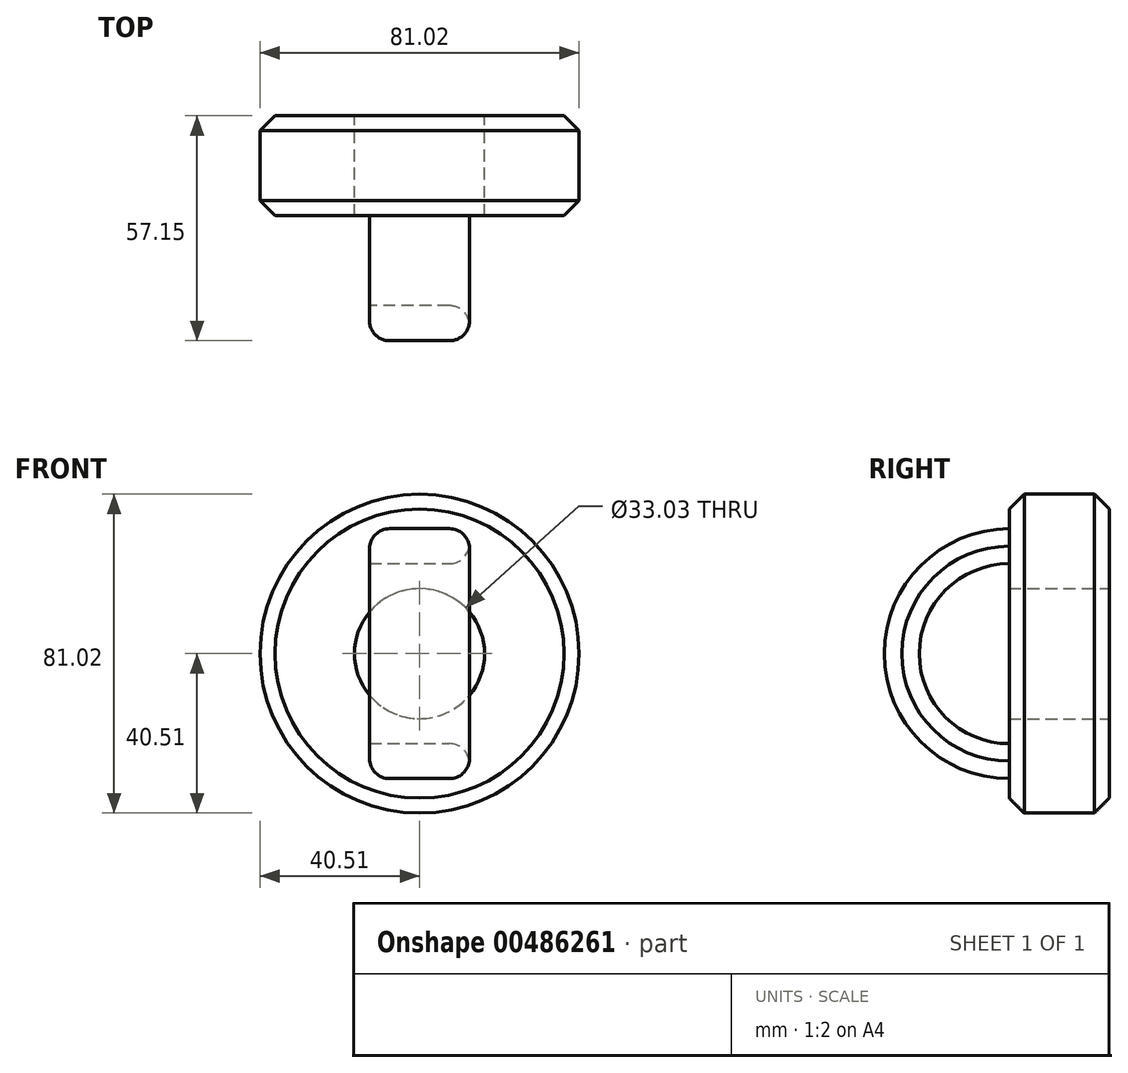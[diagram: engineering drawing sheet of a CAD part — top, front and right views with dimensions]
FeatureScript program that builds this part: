
annotation { "Feature Type Name" : "Feature", "Feature Type Description" : "" }
export const myFeature = defineFeature(function(context is Context, id is Id, definition is map)
    precondition{}
    {
        {
            var Q0;
            Q0=qCreatedBy(makeId("Front.planeOp"),FACE);
            var sketch = newSketch(context, id + "F0", { "sketchPlane" : qUnion([Q0])});
            skCircle(sketch, "E0", {"center": v(0, 0) * mm, "radius": 16.52 * mm});
            skCircle(sketch, "E1", {"center": v(0, 0) * mm, "radius": 40.51 * mm});
            skSolve(sketch);
        }
        {
            var Q0;
            Q0 = qSketchRegion(id + "F0", true);
            extrude(context, id + "F1", {"entities" : qUnion([Q0]), "depth" : 25.4 * mm});
        }
        {
            var Q0;
            Q0=makeQuery(id+"F1.opExtrude","CAP_FACE",FACE,{"disambiguationData":[OSD([sQuery(id+"F0.wireOp",EDGE,"E0"),sQuery(id+"F0.wireOp",EDGE,"E1")])],"isStart":false});
            var sketch = newSketch(context, id + "F2", { "sketchPlane" : qUnion([Q0])});
            skLineSegment(sketch, "E2.bottom", {"start": v(-12.7, 31.75) * mm, "end": v(12.7, 31.75) * mm});
            skLineSegment(sketch, "E2.top", {"start": v(-12.7, 22.86) * mm, "end": v(12.7, 22.86) * mm});
            skLineSegment(sketch, "E2.left", {"start": v(-12.7, 31.75) * mm, "end": v(-12.7, 22.86) * mm});
            skLineSegment(sketch, "E2.right", {"start": v(12.7, 31.75) * mm, "end": v(12.7, 22.86) * mm});
            skLineSegment(sketch, "E3", {"start": v(-65.94, 0) * mm, "end": v(56.87, 0) * mm});
            skLineSegment(sketch, "E4", {"start": v(56.87, 0) * mm, "end": v(0, 0) * mm});
            skSolve(sketch);
        }
        {
            var Q0;
            Q0=makeQuery(id+"F2.imprint","IMPRINT",FACE,{"disambiguationData":[TD([[makeQuery(id+"F2.imprint","IMPRINT",EDGE,{"derivedFrom":sQuery(id+"F2.wireOp",EDGE,"E2.bottom")}),-1.0]])]});
            var Q1;
            Q1=sQuery(id+"F2.wireOp",EDGE,"E3");
            revolve(context, id + "F3", {"operationType" : NewBodyOperationType.ADD, "entities" : qUnion([Q0]), "axis" : qUnion([Q1]), "revolveType" : RevolveType.ONE_DIRECTION, "angle" : 180 * degree});
        }
        {
            var Q0;
            Q0=makeQuery(id+"F3.opRevolve","SWEPT_EDGE",EDGE,{"disambiguationData":[OSD([sQuery(id+"F2.wireOp",EDGE,"E2.top"),sQuery(id+"F2.wireOp",EDGE,"E2.right")])]});
            var Q1;
            Q1=makeQuery(id+"F3.opRevolve","SWEPT_EDGE",EDGE,{"disambiguationData":[OSD([sQuery(id+"F2.wireOp",EDGE,"E2.bottom"),sQuery(id+"F2.wireOp",EDGE,"E2.right")])]});
            var Q2;
            Q2=makeQuery(id+"F3.opRevolve","SWEPT_EDGE",EDGE,{"disambiguationData":[OSD([sQuery(id+"F2.wireOp",EDGE,"E2.bottom"),sQuery(id+"F2.wireOp",EDGE,"E2.left")])]});
            fillet(context, id + "F4", {"entities" : qUnion([Q0, Q1, Q2]), "radius" : 5.08 * mm, "tangentPropagation" : true, "allowEdgeOverflow" : false});
        }
        {
            var Q0;
            Q0=makeQuery(id+"F1.opExtrude","CAP_EDGE",EDGE,{"disambiguationData":[OSD([sQuery(id+"F0.wireOp",EDGE,"E1")])],"isStart":false});
            var Q1;
            Q1=makeQuery(id+"F1.opExtrude","CAP_EDGE",EDGE,{"disambiguationData":[OSD([sQuery(id+"F0.wireOp",EDGE,"E1")])],"isStart":true});
            chamfer(context, id + "F5", {"entities" : qUnion([Q0, Q1]), "width" : 3.8 * mm, "tangentPropagation" : true});
        }
    });
